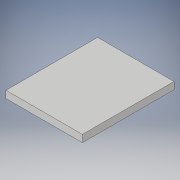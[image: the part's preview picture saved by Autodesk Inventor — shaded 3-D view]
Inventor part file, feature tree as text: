
AUTODESK INVENTOR PART (.ipt)
format: ipt  version: 2018 (Build 220112000, 112)  size: 89,088 bytes
history: native  units: in
note: dims shown in document units (in); Inventor stores cm internally (conversion verified against a paired STEP export)
features: extrude x1, sketch x1
ambient origin geometry x8: Origin, YZ Plane, XZ Plane, XY Plane, X Axis, Y Axis, Z Axis, Center Point
bodies: Solid1 (feature_tree)
feature tree (2):
  extrude  "Extrusion1"  Depth=1.9173in
  sketch  "Sketch1"  dims[d0=1.5984in d1=1.9173in d2=0.1496in d3=0.0in]
